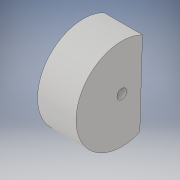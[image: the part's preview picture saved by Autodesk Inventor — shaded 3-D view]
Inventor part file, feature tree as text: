
AUTODESK INVENTOR PART (.ipt)
format: ipt  version: 2019 (Build 230136000, 136)  size: 116,224 bytes
history: native  units: in
note: dims shown in document units (in); Inventor stores cm internally (conversion verified against a paired STEP export)
features: extrude x4, sketch x4, projected_geometry x1
ambient origin geometry x8: Origin, YZ Plane, XZ Plane, XY Plane, X Axis, Y Axis, Z Axis, Center Point
bodies: Solid1 (feature_tree)
feature tree (9):
  extrude  "Extrusion1"  Depth=2.375in
  extrude  "Extrusion2"  Depth=0.25in TaperAngle=0.0deg
  extrude  "Extrusion3"  Depth=0.25in TaperAngle=0.0deg
  extrude  "Extrusion4"  Depth=0.25in TaperAngle=0.0deg
  sketch  "Sketch1"  dims[d0=2.25in d1=2.375in]
  sketch  "Sketch2"  dims[d2=1.0in d3=0.0in d4=0.25in d5=0.0in]
  projected_geometry  "Projected Loop1"
  sketch  "Sketch3"  dims[d6=2.15in d7=0.25in d8=0.0in]
  sketch  "Sketch4"  dims[d9=0.25in d10=0.25in d11=0.0in]
